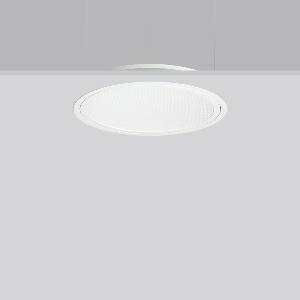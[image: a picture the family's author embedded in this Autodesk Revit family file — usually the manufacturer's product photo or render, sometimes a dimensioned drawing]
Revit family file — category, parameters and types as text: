
# Revit family: triona_round_e_312423_002_2_12_23f5
name_source: partatom
category: Lighting Fixtures
units: mm (PartAtom-declared; Revit-internal decimal feet)

## family parameters
Cut with Voids When Loaded = No
Host = Face
Light Source = No
Part Type = Normal
Room Calculation Point = No
Round Connector Dimension = Use Diameter
Shared = No

## types (1)
- TuneableWhite 846 (1 x LED Modul 846, 2700 lm, 4600)
    Apparent Load = 29 VA
    CIE Flux Codes = 58 87 97 100 100
    Color Rendering = 80
    Color Temperature = 4600
    Default Elevation = 1800 mm
    Description = Series: TRIONA round
Decorative round LED recessed surface luminaire. Cover made of sheet steel, powder-coated. Frame made of aluminium, powder-coated. Recessed ring: aluminium extrusion profile, powder coated. Light emission through a diffuser in plastic, opal/prismatic. Lightguide and diffuser made of non-yellowing plastic (PMMA). Lateral light emission (RZB SIDELITE technology) for above-average homogeneous light distribution. Tunable white versions, dynamically adjustable from 2700 K to 6500 K. Suitable for installation in cavity ceilings. Tool-free mounting system thanks to the rocker arm mechanism (patent pending). Electronic ballast included. Very easy installation thanks to Plug+Play connection. Ideal for use as part of the Human Centric Lighting concept in connection with RZB light management systems. 
Colour: traffic white, matt (RAL 9016)
Diameter: 505 mm
Height: 2 mm
Cut-out diameter: 482 mm
Recess height: 100 mm
Luminaire: recess height: 89 mm
Lamp: LED
Socket: without socket
Colour temperature: 2700K - 6500K
Colour rendering index (CRI): 80
System power: 29 W
Rated luminous flux: 2700 lm
Luminous efficiency: 93 lm/W
System power 2: 29 W
Rated luminous flux 2: 2550 lm
Luminous efficiency 2: 88 lm/W
System power 3: 30 W
Rated luminous flux 3: 2600 lm
Luminous efficiency 3: 87 lm/W
Control gear: Converter, dimmable, DALI
Protection class: I
Type of protection: IP 40
    Height = 0 mm  [stored 0 ft]
    Lamp = 1 x LED Modul 846
    Lamp Light Flux = 2700 lm
    Lamp count = 1
    Length = 505 mm
    Lifetime = 50000 h
    Luminous efficacy = 93 lm/W
    Manufacturer = RZB
    ModVariant = No
    Model = 312423.002.2.12
    Mounting Place = Ceiling
    Mounting Type = Recessed
    Number of Poles = 1
    OnlyDefault = Yes
    Power Factor = 1
    Product Name = TRIONA round E
    Product group = Recessed modular luminaires
    ProductGroupID = 406
    Protection Class = Protection class I
    Protection Degree = IP 20
    RLX_Detail_Level = 1
    RLX_Emergency_Light_Flux = 0 lm
    RLX_Emergency_Type = 0
    RLX_Emergency_Type_DB = No
    RlxData = <blob elided: 31681 chars, md5=cdbc095c>
    Socket = socket
    Standby Power = 0 W
    System Light Flux = 2700 lm
    System Power = 29 W
    Type Comments = TuneableWhite 846
    Type Image = 312423.002.12.jpg
    URL = http://relux.com
    VarID = tuneablewhite_846
    Voltage = 230 V
    Voltage Range = 220-240 V
    Weight = 0.00 kg
    Width = 0 mm  [stored 0 ft]

note: [stored X ft] marks values corroborated as IEEE doubles in the binary element streams (Revit-internal decimal feet)

## geometry (parser evidence)
native form markers: Blend x4, Sweep x9
no freeform markers — native parametric forms only
